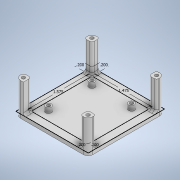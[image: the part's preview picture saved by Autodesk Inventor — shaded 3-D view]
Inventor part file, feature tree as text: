
AUTODESK INVENTOR PART (.ipt)
format: ipt  version: 2020 (Build 240168000, 168)  size: 249,856 bytes
history: native  units: in
note: dims shown in document units (in); Inventor stores cm internally (conversion verified against a paired STEP export)
features: sketch x4, extrude x3, hole x2, fillet x2
ambient origin geometry x8: Origin, YZ Plane, XZ Plane, XY Plane, X Axis, Y Axis, Z Axis, Center Point
bodies: Solid1 (feature_tree)
feature tree (11):
  sketch  "Sketch1"  dims[d0=0.2in d1=0.2in]
  extrude  "Extrusion1"  Depth=0.2in
  extrude  "Extrusion2"  Depth=1.575in
  extrude  "Extrusion3"  Depth=0.2in
  hole  "Hole1"  [1 undecoded]
  hole  "Hole2"  [1 undecoded]
  fillet  "Fillet1"  Radius=1.125in
  fillet  "Fillet2"  Radius=0.15in
  sketch  "Sketch2"  dims[d2=1.475in d3=1.575in]
  sketch  "Sketch3"  dims[d4=0.2in d5=0.2in]
  sketch  "Sketch4"  dims[d6=0.1in d7=0.0in d8=0.75in d9=0.0in d10=1.025in d11=1.125in d12=0.15in d13=0.15in d14=0.15in d15=0.15in d16=0.125in d17=0.0in d18=0.089in d19=0.75in d20=0.219in d21=0.112in d22=0.5635in d23=0.224in d24=0.0in d25=0.1in d26=0.1in d27=0.1in d28=0.089in d29=0.75in d30=0.219in d31=0.112in d32=0.5635in d33=0.224in d34=0.0in d35=0.125in d36=0.0625in]
note: 2 required parameter values undecoded (feature->parameter linkage not recoverable at this tier; creation-order binding heuristic only, values carry confidence <= 0.55)
